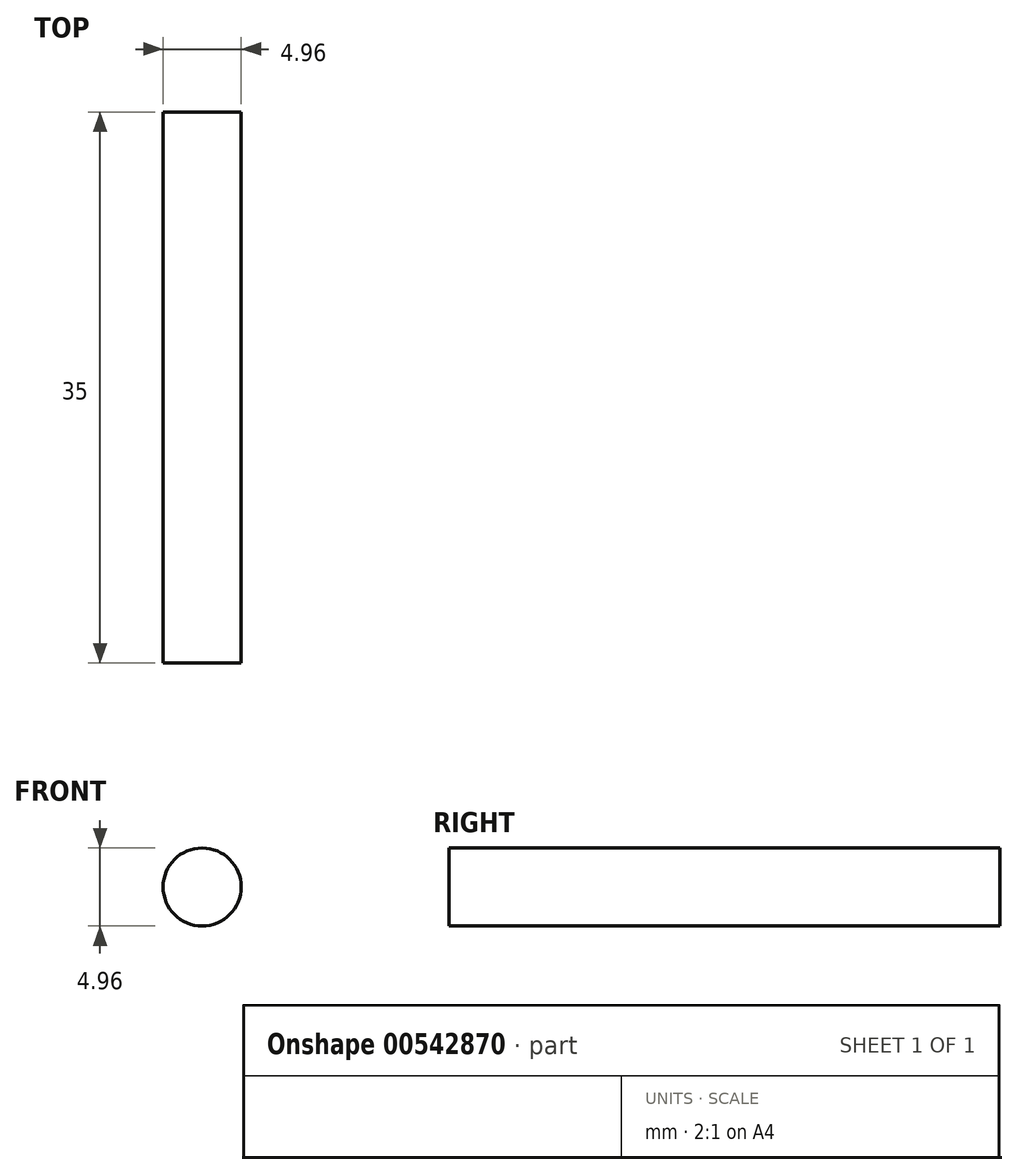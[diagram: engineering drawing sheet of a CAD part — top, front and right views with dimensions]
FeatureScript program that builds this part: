
annotation { "Feature Type Name" : "Feature", "Feature Type Description" : "" }
export const myFeature = defineFeature(function(context is Context, id is Id, definition is map)
    precondition{}
    {
        {
            var Q0;
            Q0=qCreatedBy(makeId("Front.planeOp"),FACE);
            var sketch = newSketch(context, id + "F0", { "sketchPlane" : qUnion([Q0])});
            skCircle(sketch, "E0", {"center": v(-41.43, 23) * mm, "radius": 2.48 * mm});
            skSolve(sketch);
        }
        {
            var Q0;
            Q0=makeQuery(id+"F0.imprint","IMPRINT",FACE,{"disambiguationData":[TD([[makeQuery(id+"F0.imprint","IMPRINT",EDGE,{"derivedFrom":sQuery(id+"F0.wireOp",EDGE,"E0")}),1.0]])]});
            extrude(context, id + "F1", {"entities" : qUnion([Q0]), "depth" : 35 * mm, "offsetDistance" : 25 * mm});
        }
    });
